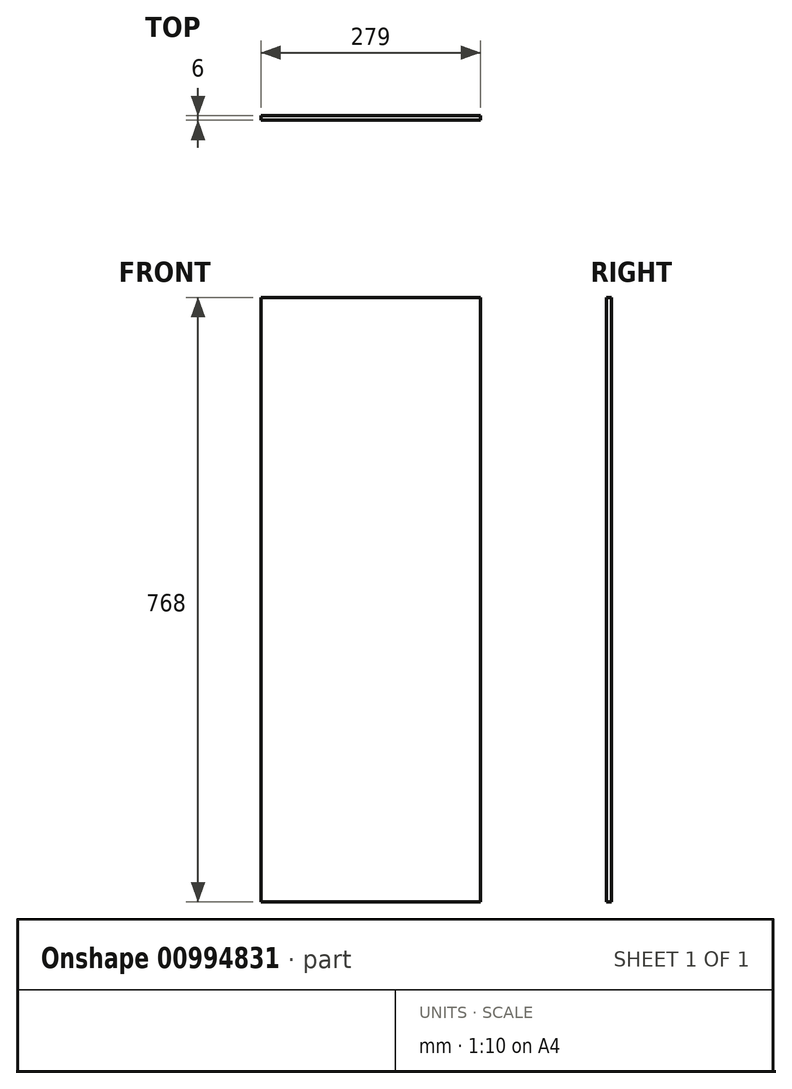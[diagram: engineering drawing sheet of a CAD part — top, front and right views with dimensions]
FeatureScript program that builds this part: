
annotation { "Feature Type Name" : "Feature", "Feature Type Description" : "" }
export const myFeature = defineFeature(function(context is Context, id is Id, definition is map)
    precondition{}
    {
        {
            var Q0;
            Q0=qCreatedBy(makeId("Front.planeOp"),FACE);
            var sketch = newSketch(context, id + "F0", { "sketchPlane" : qUnion([Q0])});
            skLineSegment(sketch, "E0.bottom", {"start": v(0, 0) * mm, "end": v(279, 0) * mm});
            skLineSegment(sketch, "E0.top", {"start": v(0, 768) * mm, "end": v(279, 768) * mm});
            skLineSegment(sketch, "E0.left", {"start": v(0, 0) * mm, "end": v(0, 768) * mm});
            skLineSegment(sketch, "E0.right", {"start": v(279, 0) * mm, "end": v(279, 768) * mm});
            skSolve(sketch);
        }
        {
            var Q0;
            Q0=qSketchRegion(id+"F0",true);
            extrude(context, id + "F1", {"entities" : qUnion([Q0]), "depth" : 6 * mm});
        }
    });
